# Revit family: KingswayGroup_ElctrcStrksAndFcplts_SecureElectricStrikeHousing
name_source: partatom
category: Specialty Equipment
units: mm (PartAtom-declared; Revit-internal decimal feet)

## family parameters
Always vertical = No
Cut with Voids When Loaded = No
Part Type = Normal
Room Calculation Point = No
Round Connector Dimension = Use Diameter
Shared = No
Work Plane-Based = No

## types (1)
- KingswayGroup_ElctrcStrksAndFcplts_SecureElectricStrikeHousing
    AssetType = Fixed
    BIMObjectName = KingswayGroup_ElectricStrikesAndFaceplates_SecureElectricStrikeHousing
    Category = Pr_75_30_27_26:Electric strikes and faceplates
    Color = For full range of available finishes and colours, contact Kingsway Group
    Default Elevation = 0 mm  [stored 0 ft]
    Description = High Secure Electric Strike Housing
    DurationUnit = year
    Features = A high-strength housing for the KG240 High Secure Electric Strike Release for greater durability and easier maintenance.
    Finish = For full range of available finishes and colours, contact Kingsway Group
    IfcExportAs = IfcDiscreteAccessoryType
    IfcExportType = USERDEFINED
    Manufacturer = Kingsway Group
    ManufacturerName = Kingsway Group
    ManufacturerURL = https://kingswaygroupglobal.com
    Material = For full range of available material, contact Kingsway Group
    Model = KG245
    ModelNumber = KG245
    ModelReference = Secure Electric Strike Housing
    Name = ElectricStrikesAndFaceplates_SecureElectricStrikeHousing_KG245_KingswayGroup
    PlateMaterial = NBS_Concept
    ProductInformation = https://kingswaygroupglobal.com
    Size = 43/48 x 260 x 44 mm
    URL = https://kingswaygroupglobal.com
    Uniclass2015Code = Pr_75_30_27_26
    Uniclass2015Title = Electric strikes and faceplates
    Uniclass2015Version = Products v1.36
    Version = 1
    WarrantyDescription = 5-Year Guarantee *For faulty manufacture and not for damage
    WarrantyDurationParts = 5
    WarrantyDurationUnit = year

note: [stored X ft] marks values corroborated as IEEE doubles in the binary element streams (Revit-internal decimal feet)

## geometry (parser evidence)
native form markers: Sweep x2
no freeform markers — native parametric forms only
